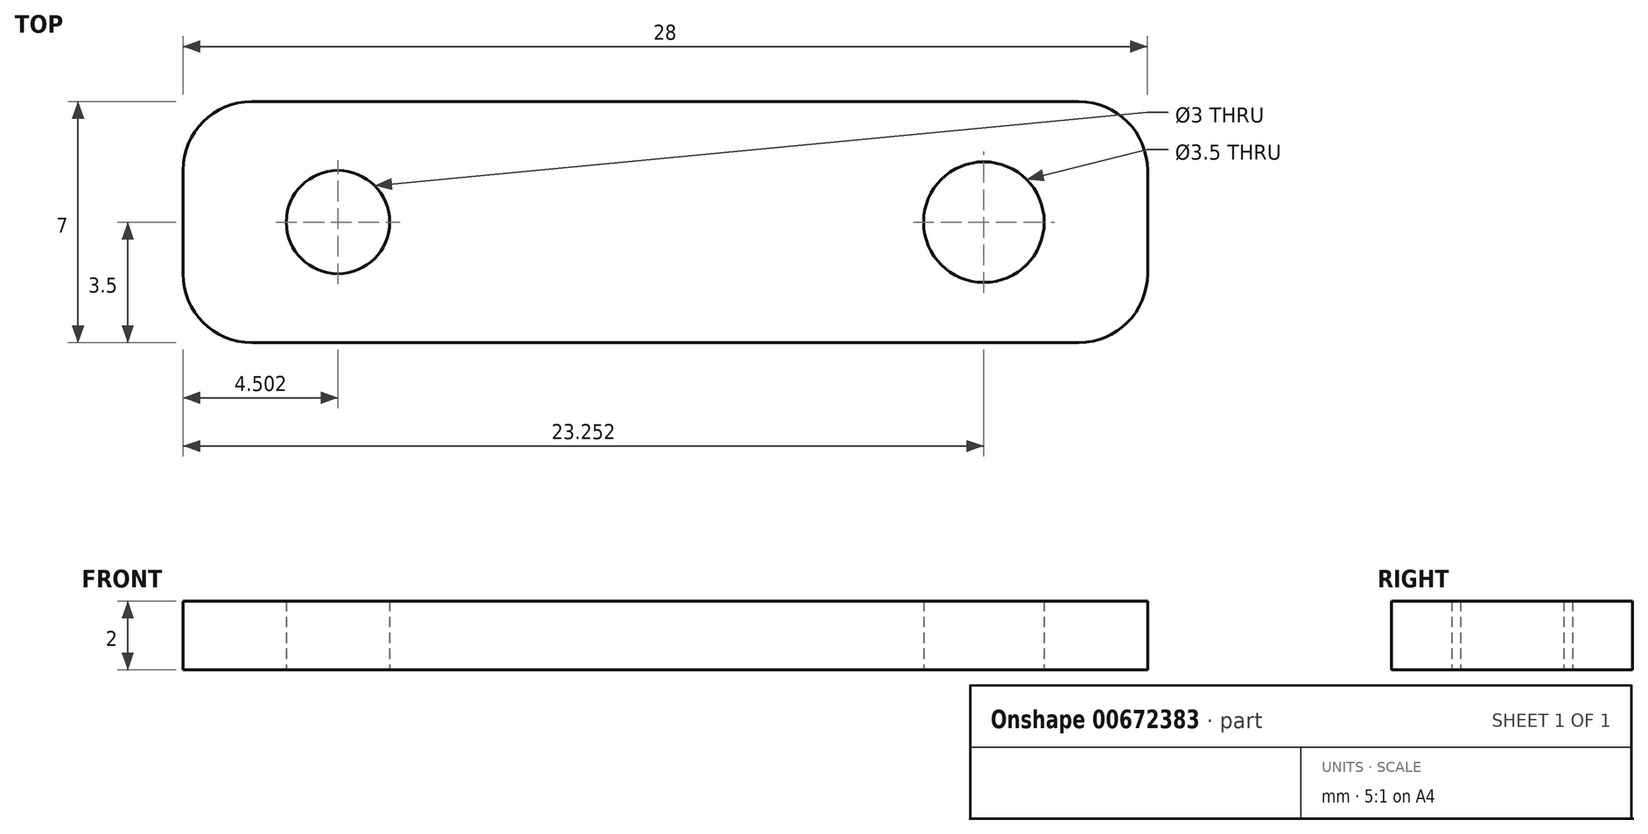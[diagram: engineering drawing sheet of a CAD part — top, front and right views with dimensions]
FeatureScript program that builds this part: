
annotation { "Feature Type Name" : "Feature", "Feature Type Description" : "" }
export const myFeature = defineFeature(function(context is Context, id is Id, definition is map)
    precondition{}
    {
        {
            var Q0;
            Q0=qCreatedBy(makeId("Top.planeOp"),FACE);
            var sketch = newSketch(context, id + "F0", { "sketchPlane" : qUnion([Q0])});
            skLineSegment(sketch, "E0.bottom", {"start": v(-3.2, 3.7) * mm, "end": v(24.8, 3.7) * mm});
            skLineSegment(sketch, "E0.top", {"start": v(-3.2, -3.3) * mm, "end": v(24.8, -3.3) * mm});
            skLineSegment(sketch, "E0.left", {"start": v(-3.2, 3.7) * mm, "end": v(-3.2, -3.3) * mm});
            skLineSegment(sketch, "E0.right", {"start": v(24.8, 3.7) * mm, "end": v(24.8, -3.3) * mm});
            skCircle(sketch, "E1", {"center": v(1.3, 0.2) * mm, "radius": 1.5 * mm});
            skCircle(sketch, "E2", {"center": v(20.04, 0.2) * mm, "radius": 1.75 * mm});
            skSolve(sketch);
        }
        {
            var Q0;
            Q0=makeQuery(id+"F0.imprint","IMPRINT",FACE,{"disambiguationData":[TD([[makeQuery(id+"F0.imprint","IMPRINT",EDGE,{"derivedFrom":sQuery(id+"F0.wireOp",EDGE,"E0.bottom")}),-1.0]])]});
            extrude(context, id + "F1", {"entities" : qUnion([Q0]), "depth" : 2 * mm, "offsetDistance" : 25 * mm});
        }
        {
            var Q0;
            Q0=makeQuery(id+"F1.opExtrude","SWEPT_EDGE",EDGE,{"disambiguationData":[OSD([sQuery(id+"F0.wireOp",EDGE,"E0.bottom"),sQuery(id+"F0.wireOp",EDGE,"E0.left")])]});
            var Q1;
            Q1=makeQuery(id+"F1.opExtrude","SWEPT_EDGE",EDGE,{"disambiguationData":[OSD([sQuery(id+"F0.wireOp",EDGE,"E0.top"),sQuery(id+"F0.wireOp",EDGE,"E0.left")])]});
            var Q2;
            Q2=makeQuery(id+"F1.opExtrude","SWEPT_EDGE",EDGE,{"disambiguationData":[OSD([sQuery(id+"F0.wireOp",EDGE,"E0.top"),sQuery(id+"F0.wireOp",EDGE,"E0.right")])]});
            var Q3;
            Q3=makeQuery(id+"F1.opExtrude","SWEPT_EDGE",EDGE,{"disambiguationData":[OSD([sQuery(id+"F0.wireOp",EDGE,"E0.bottom"),sQuery(id+"F0.wireOp",EDGE,"E0.right")])]});
            fillet(context, id + "F2", {"entities" : qUnion([Q0, Q1, Q2, Q3]), "radius" : 2 * mm, "tangentPropagation" : true, "allowEdgeOverflow" : false});
        }
    });
